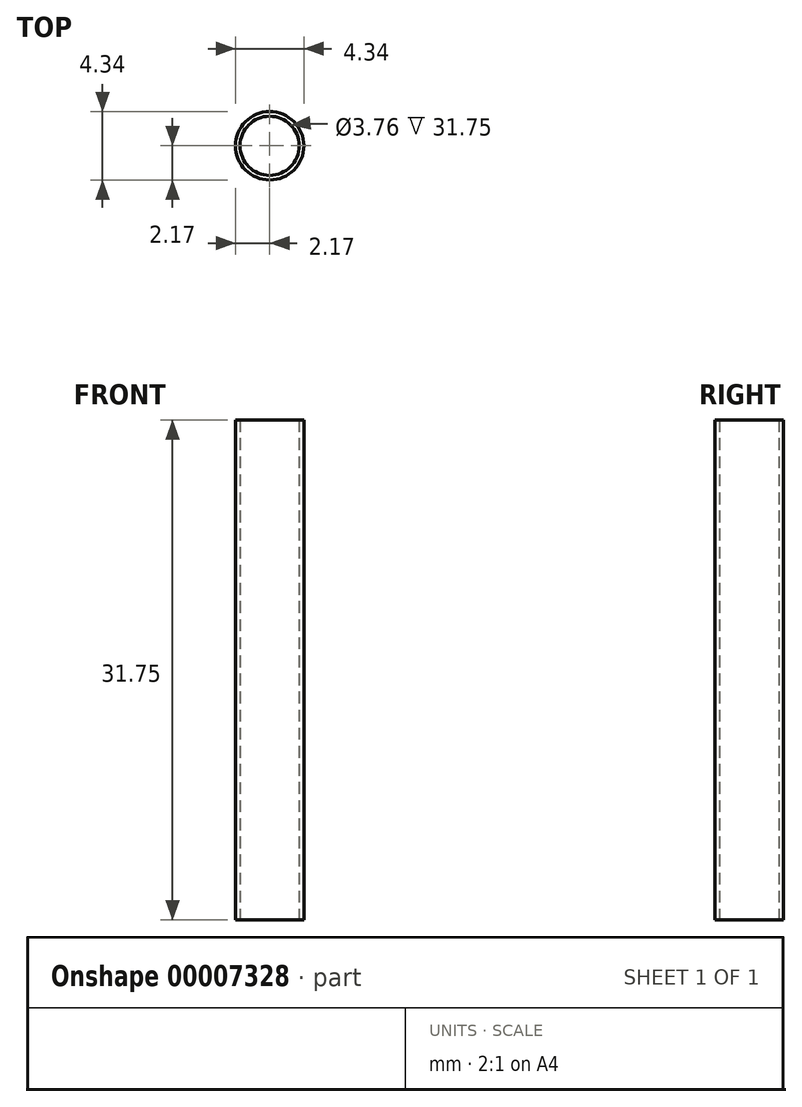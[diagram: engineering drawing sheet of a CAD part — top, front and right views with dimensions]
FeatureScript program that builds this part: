
annotation { "Feature Type Name" : "Feature", "Feature Type Description" : "" }
export const myFeature = defineFeature(function(context is Context, id is Id, definition is map)
    precondition{}
    {
        {
            var Q0;
            Q0=qCreatedBy(makeId("Front.planeOp"),FACE);
            var sketch = newSketch(context, id + "F0", { "sketchPlane" : qUnion([Q0])});
            skLineSegment(sketch, "E0.bottom", {"start": v(1.88, 0) * mm, "end": v(2.17, 0) * mm});
            skLineSegment(sketch, "E0.top", {"start": v(1.88, 31.75) * mm, "end": v(2.17, 31.75) * mm});
            skLineSegment(sketch, "E0.left", {"start": v(1.88, 0) * mm, "end": v(1.88, 31.75) * mm});
            skLineSegment(sketch, "E0.right", {"start": v(2.17, 0) * mm, "end": v(2.17, 31.75) * mm});
            skLineSegment(sketch, "E1", {"start": v(1.88, 0) * mm, "end": v(0, 0) * mm});
            skLineSegment(sketch, "E2", {"start": v(0, 0) * mm, "end": v(0, 31.75) * mm});
            skSolve(sketch);
        }
        {
            var Q0;
            Q0=qSketchRegion(id+"F0",true);
            var Q1;
            Q1=sQuery(id+"F0.wireOp",EDGE,"E2");
            revolve(context, id + "F1", {"entities" : qUnion([Q0]), "axis" : qUnion([Q1]), "revolveType" : RevolveType.FULL});
        }
    });
